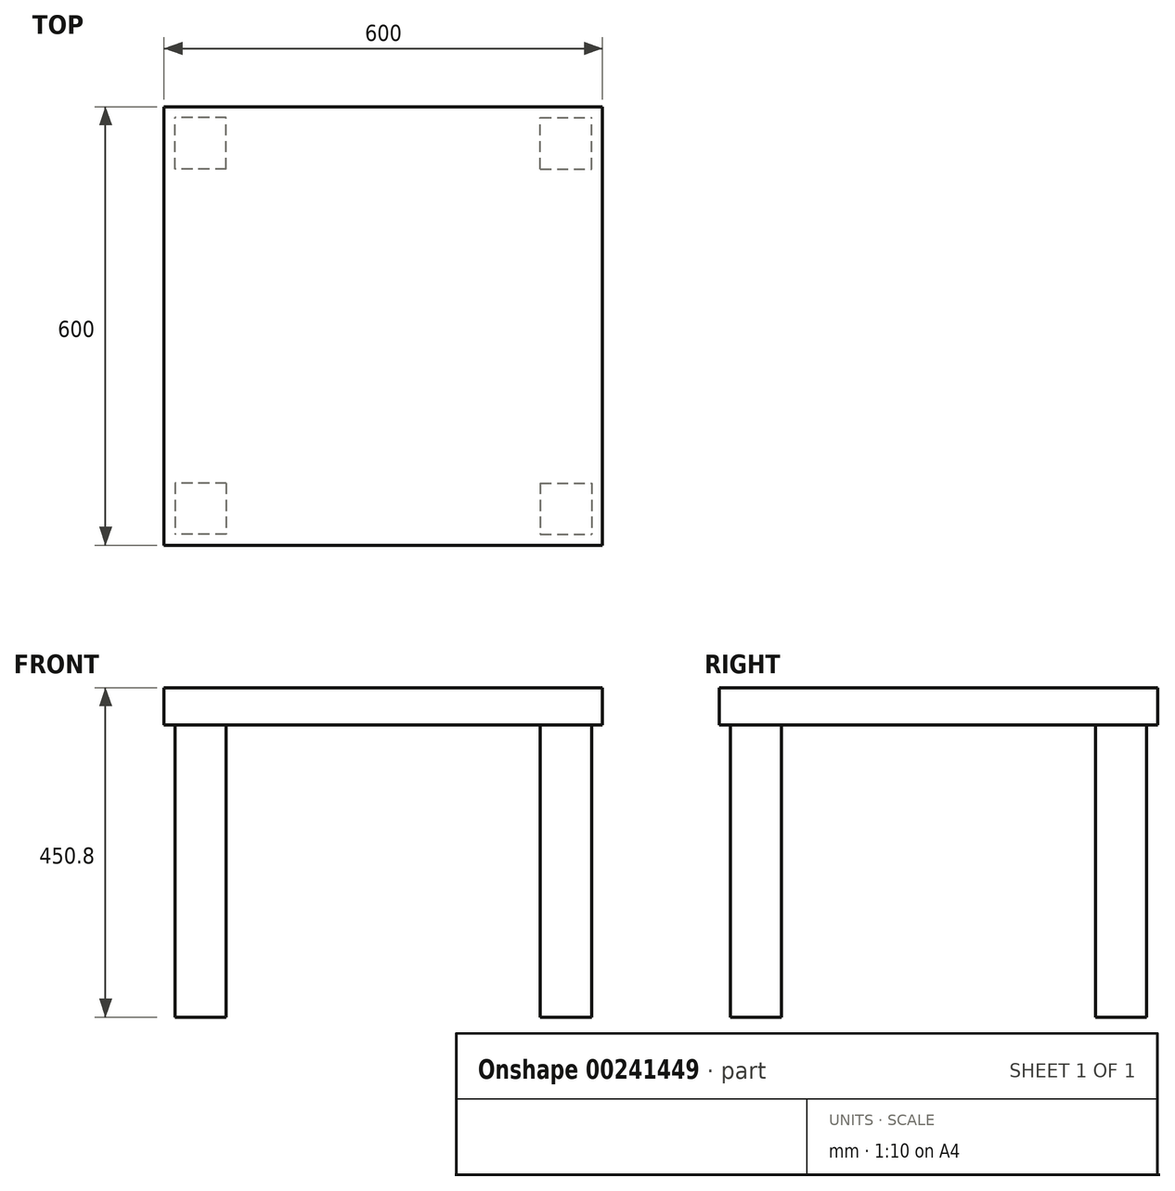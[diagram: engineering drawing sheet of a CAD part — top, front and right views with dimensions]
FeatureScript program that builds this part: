
annotation { "Feature Type Name" : "Feature", "Feature Type Description" : "" }
export const myFeature = defineFeature(function(context is Context, id is Id, definition is map)
    precondition{}
    {
        {
            var Q0;
            Q0=qCreatedBy(makeId("Top.planeOp"),FACE);
            var sketch = newSketch(context, id + "F0", { "sketchPlane" : qUnion([Q0])});
            skLineSegment(sketch, "E0.bottom", {"start": v(-300, 300) * mm, "end": v(300, 300) * mm});
            skLineSegment(sketch, "E0.top", {"start": v(-300, -300) * mm, "end": v(300, -300) * mm});
            skLineSegment(sketch, "E0.left", {"start": v(-300, 300) * mm, "end": v(-300, -300) * mm});
            skLineSegment(sketch, "E0.right", {"start": v(300, 300) * mm, "end": v(300, -300) * mm});
            skSolve(sketch);
        }
        {
            var Q0;
            Q0=qSketchRegion(id+"F0",true);
            extrude(context, id + "F1", {"entities" : qUnion([Q0]), "depth" : 50.8 * mm});
        }
        {
            var Q0;
            Q0=qCreatedBy(makeId("Front.planeOp"),FACE);
            var sketch = newSketch(context, id + "F2", { "sketchPlane" : qUnion([Q0])});
            skLineSegment(sketch, "E1", {"start": v(0, -775.44) * mm, "end": v(0, 0) * mm});
            skSolve(sketch);
        }
        {
            var Q0;
            Q0=qCreatedBy(makeId("Top.planeOp"),FACE);
            var sketch = newSketch(context, id + "F3", { "sketchPlane" : qUnion([Q0])});
            skLineSegment(sketch, "E2.bottom", {"start": v(-215, -215) * mm, "end": v(-285, -215) * mm});
            skLineSegment(sketch, "E2.top", {"start": v(-215, -285) * mm, "end": v(-285, -285) * mm});
            skLineSegment(sketch, "E2.left", {"start": v(-215, -215) * mm, "end": v(-215, -285) * mm});
            skLineSegment(sketch, "E2.right", {"start": v(-285, -215) * mm, "end": v(-285, -285) * mm});
            skPoint(sketch, "E2.middle", {"position": v(-250, -250) * mm});
            skSolve(sketch);
        }
        {
            var Q0;
            Q0 = qSketchRegion(id + "F3", true);
            extrude(context, id + "F4", {"entities" : qUnion([Q0]), "oppositeDirection" : true, "depth" : 400 * mm});
        }
        {
            var Q0;
            Q0=makeQuery(id+"F4.opExtrude","SWEPT_BODY",BODY,{"disambiguationData":[OSD([sQuery(id+"F3.wireOp",EDGE,"E2.bottom"),sQuery(id+"F3.wireOp",EDGE,"E2.top"),sQuery(id+"F3.wireOp",EDGE,"E2.left"),sQuery(id+"F3.wireOp",EDGE,"E2.right")])]});
            var Q1;
            Q1=sQuery(id+"F2.wireOp",EDGE,"E1");
            circularPattern(context, id + "F5", {"entities" : qUnion([Q0]), "axis" : qUnion([Q1]), "angle" : 360 * degree, "instanceCount" : 4, "equalSpace" : true});
        }
    });
